# Revit family: RAS-C2_RFA
name_source: partatom
category: Pipe Accessories
units: mm (PartAtom-declared; Revit-internal decimal feet)

## family parameters
Always vertical = Yes
Cut with Voids When Loaded = No
Part Type = Valve - Breaks Into
Round Connector Dimension = Use Diameter
Shared = No
Work Plane-Based = No

## types (1)
- RAS-C2_013G6040
    Body Material = Danfoss Plastic White
    CenSd_NR2_6 = 12 mm  [stored 0.0393701 ft]
    CenSd_NR3_6 = 8 mm  [stored 0.0262467 ft]
    D = 10 mm
    Description = RAS-C2
    IfcExportAs = IfcActuatorType
    IfcExportType = RAS-C2
    LOD 200 = No
    LOD 350 = Yes
    Manufacturer = Danfoss
    Model = 013G6040
    NL1 = 6 mm  [stored 0.019685 ft]
    NR1 = 12 mm  [stored 0.0393701 ft]
    S1 = 2 mm  [stored 0.00656168 ft]
    S2 = 6 mm  [stored 0.019685 ft]
    Setting Range = 8 - 28 °C
    URL = https://store.danfoss.com
    VH = 82 mm
    VH1 = 4 mm  [stored 0.0131234 ft]
    VH2 = 9 mm  [stored 0.0295276 ft]
    VH3 = 40 mm  [stored 0.131234 ft]
    VH4 = 3 mm  [stored 0.00984252 ft]
    VH5 = 23 mm  [stored 0.0754593 ft]
    VH6 = 69 mm
    VR1 = 16 mm  [stored 0.0524934 ft]
    VR2 = 18 mm
    VR3 = 21 mm  [stored 0.0688976 ft]
    VR4 = 23 mm  [stored 0.0754593 ft]
    VR5 = 25 mm  [stored 0.082021 ft]
    VR6 = 24 mm  [stored 0.0787402 ft]
    VR7 = 20 mm  [stored 0.0656168 ft]
    W = 50 mm
    X = 8 mm  [stored 0.0262467 ft]

note: [stored X ft] marks values corroborated as IEEE doubles in the binary element streams (Revit-internal decimal feet)

## geometry (parser evidence)
native form markers: Sweep x3
no freeform markers — native parametric forms only
